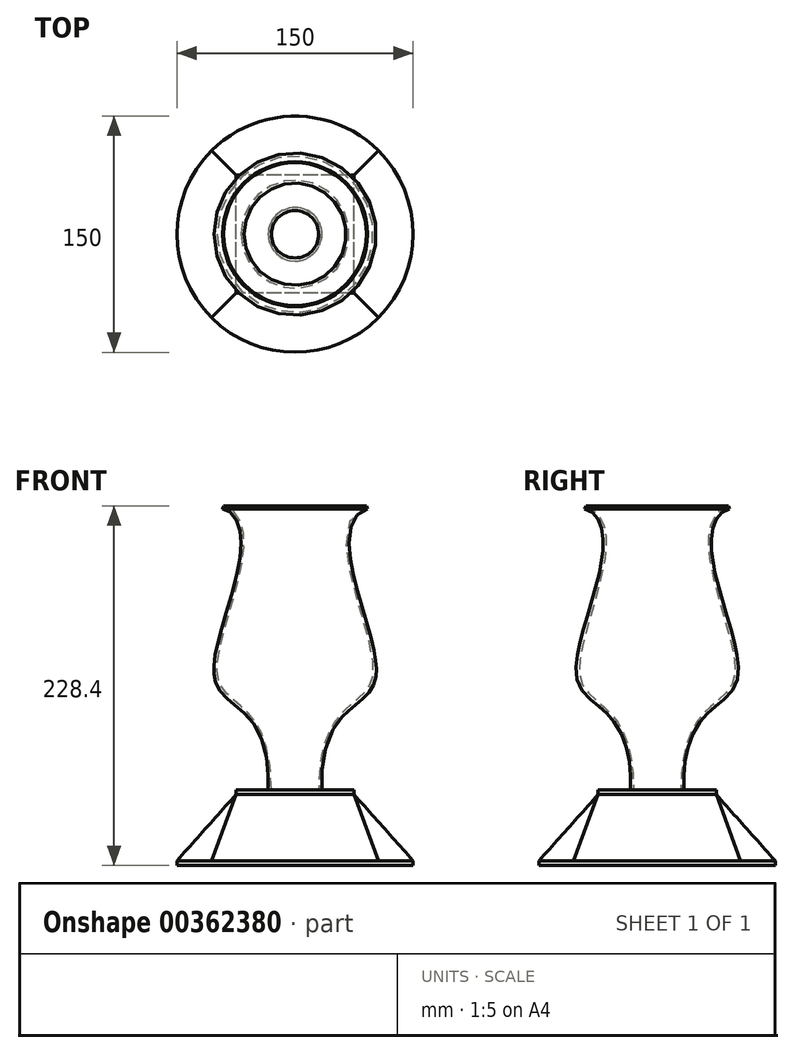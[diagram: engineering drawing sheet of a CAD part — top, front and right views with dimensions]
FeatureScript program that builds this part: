
annotation { "Feature Type Name" : "Feature", "Feature Type Description" : "" }
export const myFeature = defineFeature(function(context is Context, id is Id, definition is map)
    precondition{}
    {
        {
            var Q0;
            Q0=qCreatedBy(makeId("Top.planeOp"),FACE);
            var sketch = newSketch(context, id + "F0", { "sketchPlane" : qUnion([Q0])});
            skCircle(sketch, "E0", {"center": v(0, 0) * mm, "radius": 75 * mm});
            skSolve(sketch);
        }
        {
            var Q0;
            Q0=qCreatedBy(makeId("Top.planeOp"),FACE);
            cPlane(context, id + "F1", {"entities" : qUnion([Q0]), "cplaneType" : CPlaneType.OFFSET, "offset" : 45 * mm, "width" : 150 * mm, "height" : 150 * mm});
        }
        {
            var Q0;
            Q0=qCreatedBy(id+"F1.planeOp",FACE);
            var sketch = newSketch(context, id + "F2", { "sketchPlane" : qUnion([Q0])});
            skLineSegment(sketch, "E1.bottom", {"start": v(37.5, -37.5) * mm, "end": v(-37.5, -37.5) * mm});
            skLineSegment(sketch, "E1.top", {"start": v(37.5, 37.5) * mm, "end": v(-37.5, 37.5) * mm});
            skLineSegment(sketch, "E1.left", {"start": v(37.5, -37.5) * mm, "end": v(37.5, 37.5) * mm});
            skLineSegment(sketch, "E1.right", {"start": v(-37.5, -37.5) * mm, "end": v(-37.5, 37.5) * mm});
            skPoint(sketch, "E1.middle", {"position": v(0, 0) * mm});
            skSolve(sketch);
        }
        {
            var Q0;
            Q0=makeQuery(id+"F0.imprint","IMPRINT",FACE,{"disambiguationData":[TD([[makeQuery(id+"F0.imprint","IMPRINT",EDGE,{"derivedFrom":sQuery(id+"F0.wireOp",EDGE,"E0")}),1.0]])]});
            extrude(context, id + "F3", {"entities" : qUnion([Q0]), "depth" : 3 * mm});
        }
        {
            var Q0;
            Q0=makeQuery(id+"F2.imprint","IMPRINT",FACE,{"disambiguationData":[TD([[makeQuery(id+"F2.imprint","IMPRINT",EDGE,{"derivedFrom":sQuery(id+"F2.wireOp",EDGE,"E1.bottom")}),-1.0]])]});
            extrude(context, id + "F4", {"entities" : qUnion([Q0]), "depth" : 3 * mm});
        }
        {
            var Q0;
            Q0=makeQuery(id+"F4.opExtrude","CAP_FACE",FACE,{"disambiguationData":[OSD([sQuery(id+"F2.wireOp",EDGE,"E1.bottom"),sQuery(id+"F2.wireOp",EDGE,"E1.top"),sQuery(id+"F2.wireOp",EDGE,"E1.left"),sQuery(id+"F2.wireOp",EDGE,"E1.right")])],"isStart":false});
            var sketch = newSketch(context, id + "F5", { "sketchPlane" : qUnion([Q0])});
            skLineSegment(sketch, "E2", {"start": v(-37.5, -37.5) * mm, "end": v(37.5, 37.5) * mm, "construction": true});
            skLineSegment(sketch, "E3", {"start": v(-37.5, 37.5) * mm, "end": v(37.5, -37.5) * mm, "construction": true});
            skCircle(sketch, "E4", {"center": v(0, 0) * mm, "radius": 32.5 * mm});
            skSolve(sketch);
        }
        {
            var Q0;
            Q0=sQuery(id+"F5.wireOp",EDGE,"E2");
            cPlane(context, id + "F6", {"entities" : qUnion([Q0]), "cplaneType" : CPlaneType.LINE_ANGLE, "offset" : 0 * mm, "angle" : 90 * degree, "width" : 150 * mm, "height" : 150 * mm});
        }
        {
            var Q0;
            Q0=qCreatedBy(id+"F6.planeOp",FACE);
            var sketch = newSketch(context, id + "F7", { "sketchPlane" : qUnion([Q0])});
            skLineSegment(sketch, "E5", {"start": v(-75, 0) * mm, "end": v(-75, 3) * mm});
            skLineSegment(sketch, "E6", {"start": v(75, 3) * mm, "end": v(75, 0) * mm});
            skLineSegment(sketch, "E7.0.0", {"start": v(-53.03, 45) * mm, "end": v(0, 45) * mm});
            skLineSegment(sketch, "E7.0.1", {"start": v(0, 45) * mm, "end": v(0, 48) * mm});
            skLineSegment(sketch, "E7.0.2", {"start": v(0, 48) * mm, "end": v(-53.03, 48) * mm});
            skLineSegment(sketch, "E7.0.3", {"start": v(-53.03, 48) * mm, "end": v(-53.03, 45) * mm});
            skFitSpline(sketch, "E8", {"points": [v(-75, 3) * mm, v(-53.03, 45) * mm], "startDerivative": vector(65.36, 41.68) * mm, "endDerivative": vector(2.59, 57.66) * mm});
            skFitSpline(sketch, "E9.MirrorCS", {"points": [v(75, 3) * mm, v(53.03, 45) * mm], "startDerivative": vector(-65.36, 41.68) * mm, "endDerivative": vector(-2.59, 57.66) * mm});
            skFitSpline(sketch, "E10.MirrorCS", {"points": [v(75, 3) * mm, v(53.03, 45) * mm], "startDerivative": vector(-65.36, 41.68) * mm, "endDerivative": vector(-2.59, 57.66) * mm});
            skFitSpline(sketch, "E11.MirrorCS", {"points": [v(75, 3) * mm, v(53.03, 45) * mm], "startDerivative": vector(-65.36, 41.68) * mm, "endDerivative": vector(-2.59, 57.66) * mm});
            skFitSpline(sketch, "E12.MirrorCS", {"points": [v(75, 3) * mm, v(53.03, 45) * mm], "startDerivative": vector(-65.36, 41.68) * mm, "endDerivative": vector(-2.59, 57.66) * mm});
            skLineSegment(sketch, "E13.MirrorCS", {"start": v(75, 0) * mm, "end": v(75, 3) * mm});
            skSolve(sketch);
        }
        {
            var Q1;
            Q1=makeQuery(id+"F3.opExtrude","CAP_FACE",FACE,{"disambiguationData":[OSD([sQuery(id+"F0.wireOp",EDGE,"E0")])],"isStart":false});
            var Q2;
            Q2=makeQuery(id+"F4.opExtrude","CAP_FACE",FACE,{"disambiguationData":[OSD([sQuery(id+"F2.wireOp",EDGE,"E1.bottom"),sQuery(id+"F2.wireOp",EDGE,"E1.top"),sQuery(id+"F2.wireOp",EDGE,"E1.left"),sQuery(id+"F2.wireOp",EDGE,"E1.right")])],"isStart":true});
            var Q3;
            Q3=sQuery(id+"F2rMSPdL2XQpfkd_2.2.F7.wireOp",EDGE,"E12.MirrorCS");
            var Q4;
            Q4=sQuery(id+"F2rMSPdL2XQpfkd_2.3.F7.wireOp",EDGE,"E12.MirrorCS");
            var Q5;
            Q5=sQuery(id+"F2rMSPdL2XQpfkd_2.2.F7.wireOp",EDGE,"E8");
            var Q6;
            Q6=sQuery(id+"F2rMSPdL2XQpfkd_2.3.F7.wireOp",EDGE,"E8");
            loft(context, id + "F8", {"operationType" : NewBodyOperationType.ADD, "addGuides" : true, "sheetProfilesArray" : [{ "sheetProfileEntities" : qUnion([Q1]) }, { "sheetProfileEntities" : qUnion([Q2]) }], "guidesArray" : [{ "guideEntities" : qUnion([Q3]), "guideDerivativeType" : LoftGuideDerivativeType.DEFAULT, "guideDerivativeMagnitude" : 1 }, { "guideEntities" : qUnion([Q4]), "guideDerivativeType" : LoftGuideDerivativeType.DEFAULT, "guideDerivativeMagnitude" : 1 }, { "guideEntities" : qUnion([Q5]), "guideDerivativeType" : LoftGuideDerivativeType.DEFAULT, "guideDerivativeMagnitude" : 1 }, { "guideEntities" : qUnion([Q6]), "guideDerivativeType" : LoftGuideDerivativeType.DEFAULT, "guideDerivativeMagnitude" : 1 }]});
        }
        {
            var Q0;
            Q0=qCreatedBy(makeId("Front.planeOp"),FACE);
            var sketch = newSketch(context, id + "F9", { "sketchPlane" : qUnion([Q0])});
            skLineSegment(sketch, "E14.0", {"start": v(-32.5, 48) * mm, "end": v(32.5, 48) * mm});
            skFitSpline(sketch, "E15", {"points": [v(15.06, 48) * mm, v(49.5, 122.26) * mm, v(45.35, 228.4) * mm], "startDerivative": vector(0, 380.63) * mm, "endDerivative": vector(180.84, 67.09) * mm});
            skFitSpline(sketch, "E16.0", {"points": [v(17.06, 48) * mm, v(17.06, 55.83) * mm, v(18.22, 69.04) * mm, v(22.44, 82.9) * mm, v(28.2, 92.37) * mm, v(33.63, 97.92) * mm, v(38.01, 101.7) * mm, v(41.22, 104.38) * mm, v(44.25, 107.1) * mm, v(46.97, 110.06) * mm, v(49.24, 113.48) * mm, v(50.59, 116.82) * mm, v(51.26, 119.84) * mm, v(51.54, 122.29) * mm, v(51.6, 124.91) * mm, v(51.4, 128.63) * mm, v(50.73, 133.65) * mm, v(49.36, 140.23) * mm, v(47.57, 147.26) * mm, v(44.81, 157.08) * mm, v(41, 169.94) * mm, v(36.9, 185.38) * mm, v(34.76, 197.43) * mm, v(34.34, 206.05) * mm, v(34.77, 211.87) * mm, v(36.05, 216.9) * mm, v(38.23, 221.03) * mm, v(41.4, 224.29) * mm, v(44.33, 225.89) * mm, v(46.05, 226.52) * mm]});
            skLineSegment(sketch, "E17", {"start": v(46.05, 226.52) * mm, "end": v(45.35, 228.4) * mm});
            skSolve(sketch);
        }
        {
            var Q0;
            {var subQ0=sQuery(id+"F9.wireOp",EDGE,"E15");Q0=makeQuery(id+"F9.imprint","IMPRINT",FACE,{"disambiguationData":[TD([[makeQuery(id+"F9.imprint","IMPRINT",EDGE,{"derivedFrom":subQ0}),-1.0]])]});}
            var Q1;
            Q1=sQuery(id+"F5.wireOp",EDGE,"E4");
            revolve(context, id + "F10", {"operationType" : NewBodyOperationType.ADD, "entities" : qUnion([Q0]), "axis" : qUnion([Q1]), "revolveType" : RevolveType.FULL});
        }
    });
